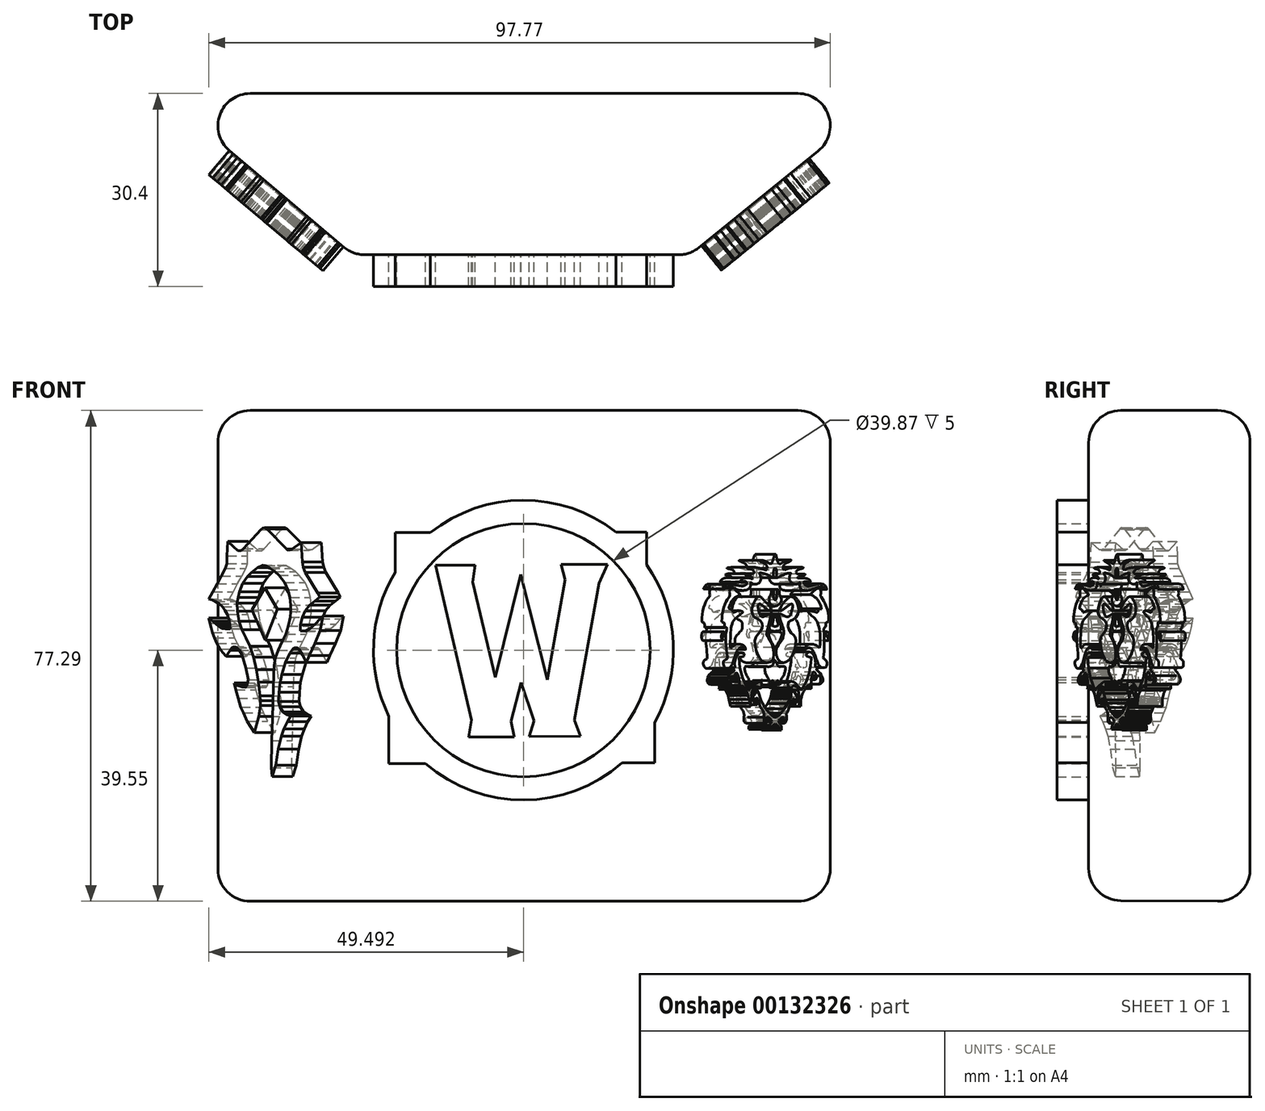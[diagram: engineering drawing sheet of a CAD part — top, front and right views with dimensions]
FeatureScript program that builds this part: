
annotation { "Feature Type Name" : "Feature", "Feature Type Description" : "" }
export const myFeature = defineFeature(function(context is Context, id is Id, definition is map)
    precondition{}
    {
        {
            var Q0;
            Q0=qCreatedBy(makeId("Front.planeOp"),FACE);
            var sketch = newSketch(context, id + "F0", { "sketchPlane" : qUnion([Q0])});
            skLineSegment(sketch, "E0.bottom", {"start": v(-46.33, 37.74) * mm, "end": v(68.1, 37.74) * mm});
            skLineSegment(sketch, "E0.top", {"start": v(-46.33, -39.59) * mm, "end": v(68.1, -39.59) * mm});
            skLineSegment(sketch, "E0.left", {"start": v(-46.33, 37.74) * mm, "end": v(-46.33, -39.59) * mm});
            skLineSegment(sketch, "E0.right", {"start": v(68.1, 37.74) * mm, "end": v(68.1, -39.59) * mm});
            skSolve(sketch);
        }
        {
            var Q0;
            Q0=makeQuery(id+"F0.imprint","IMPRINT",FACE,{"disambiguationData":[TD([[makeQuery(id+"F0.imprint","IMPRINT",EDGE,{"derivedFrom":sQuery(id+"F0.wireOp",EDGE,"E0.bottom")}),-1.0]])]});
            cPlane(context, id + "F1", {"entities" : qUnion([Q0]), "cplaneType" : CPlaneType.OFFSET, "offset" : 25.4 * mm, "width" : 152.4 * mm, "height" : 152.4 * mm});
        }
        {
            var Q0;
            Q0=qCreatedBy(id+"F1.planeOp",FACE);
            var sketch = newSketch(context, id + "F2", { "sketchPlane" : qUnion([Q0])});
            skLineSegment(sketch, "E1.bottom", {"start": v(-16.23, 37.74) * mm, "end": v(36.74, 37.74) * mm});
            skLineSegment(sketch, "E1.top", {"start": v(-16.23, -39.4) * mm, "end": v(36.74, -39.4) * mm});
            skLineSegment(sketch, "E1.left", {"start": v(-16.23, 37.74) * mm, "end": v(-16.23, -39.4) * mm});
            skLineSegment(sketch, "E1.right", {"start": v(36.74, 37.74) * mm, "end": v(36.74, -39.4) * mm});
            skSolve(sketch);
        }
        {
            var Q0;
            Q0=makeQuery(id+"F0.imprint","IMPRINT",FACE,{"disambiguationData":[TD([[makeQuery(id+"F0.imprint","IMPRINT",EDGE,{"derivedFrom":sQuery(id+"F0.wireOp",EDGE,"E0.bottom")}),-1.0]])]});
            var Q1;
            Q1=makeQuery(id+"F2.imprint","IMPRINT",FACE,{"disambiguationData":[TD([[makeQuery(id+"F2.imprint","IMPRINT",EDGE,{"derivedFrom":sQuery(id+"F2.wireOp",EDGE,"E1.bottom")}),-1.0]])]});
            loft(context, id + "F3", {"sheetProfilesArray" : [{ "sheetProfileEntities" : qUnion([Q0]) }, { "sheetProfileEntities" : qUnion([Q1]) }]});
        }
        {
            var Q0;
            Q0=makeQuery(id+"F3.opLoft","MID_CAP_EDGE",EDGE,{"disambiguationData":[OSD([sQuery(id+"F2.wireOp",EDGE,"E1.bottom"),sQuery(id+"F2.wireOp",EDGE,"E1.top"),sQuery(id+"F2.wireOp",EDGE,"E1.left")])],"capPos":1.0});
            var Q1;
            Q1=makeQuery(id+"F3.opLoft","MID_CAP_EDGE",EDGE,{"disambiguationData":[OSD([sQuery(id+"F2.wireOp",EDGE,"E1.bottom"),sQuery(id+"F2.wireOp",EDGE,"E1.top"),sQuery(id+"F2.wireOp",EDGE,"E1.right")])],"capPos":1.0});
            var Q2;
            Q2=makeQuery(id+"F3.opLoft","MID_CAP_EDGE",EDGE,{"disambiguationData":[OSD([sQuery(id+"F2.wireOp",EDGE,"E1.bottom"),sQuery(id+"F2.wireOp",EDGE,"E1.left"),sQuery(id+"F2.wireOp",EDGE,"E1.right")])],"capPos":1.0});
            var Q3;
            Q3=makeQuery(id+"F3.opLoft","SWEPT_EDGE",EDGE,{"disambiguationData":[OSD([sQuery(id+"F0.wireOp",EDGE,"E0.bottom"),sQuery(id+"F0.wireOp",EDGE,"E0.left"),sQuery(id+"F2.wireOp",EDGE,"E1.bottom"),sQuery(id+"F2.wireOp",EDGE,"E1.left")])]});
            var Q4;
            Q4=makeQuery(id+"F3.opLoft","SWEPT_EDGE",EDGE,{"disambiguationData":[OSD([sQuery(id+"F0.wireOp",EDGE,"E0.bottom"),sQuery(id+"F0.wireOp",EDGE,"E0.right"),sQuery(id+"F2.wireOp",EDGE,"E1.bottom"),sQuery(id+"F2.wireOp",EDGE,"E1.right")])]});
            var Q5;
            Q5=makeQuery(id+"F3.opLoft","SWEPT_EDGE",EDGE,{"disambiguationData":[OSD([sQuery(id+"F0.wireOp",EDGE,"E0.top"),sQuery(id+"F0.wireOp",EDGE,"E0.left"),sQuery(id+"F2.wireOp",EDGE,"E1.top"),sQuery(id+"F2.wireOp",EDGE,"E1.left")])]});
            var Q6;
            Q6=makeQuery(id+"F3.opLoft","MID_CAP_EDGE",EDGE,{"disambiguationData":[OSD([sQuery(id+"F2.wireOp",EDGE,"E1.top"),sQuery(id+"F2.wireOp",EDGE,"E1.left"),sQuery(id+"F2.wireOp",EDGE,"E1.right")])],"capPos":1.0});
            var Q7;
            Q7=makeQuery(id+"F3.opLoft","SWEPT_EDGE",EDGE,{"disambiguationData":[OSD([sQuery(id+"F0.wireOp",EDGE,"E0.top"),sQuery(id+"F0.wireOp",EDGE,"E0.right"),sQuery(id+"F2.wireOp",EDGE,"E1.top"),sQuery(id+"F2.wireOp",EDGE,"E1.right")])]});
            var Q8;
            Q8=makeQuery(id+"F3.opLoft","MID_CAP_EDGE",EDGE,{"disambiguationData":[OSD([sQuery(id+"F0.wireOp",EDGE,"E0.bottom"),sQuery(id+"F0.wireOp",EDGE,"E0.top"),sQuery(id+"F0.wireOp",EDGE,"E0.right")])],"capPos":0.0});
            var Q9;
            Q9=makeQuery(id+"F3.opLoft","MID_CAP_EDGE",EDGE,{"disambiguationData":[OSD([sQuery(id+"F0.wireOp",EDGE,"E0.bottom"),sQuery(id+"F0.wireOp",EDGE,"E0.top"),sQuery(id+"F0.wireOp",EDGE,"E0.left")])],"capPos":0.0});
            var Q10;
            Q10=makeQuery(id+"F3.opLoft","MID_CAP_EDGE",EDGE,{"disambiguationData":[OSD([sQuery(id+"F0.wireOp",EDGE,"E0.bottom"),sQuery(id+"F0.wireOp",EDGE,"E0.left"),sQuery(id+"F0.wireOp",EDGE,"E0.right")])],"capPos":0.0});
            var Q11;
            Q11=makeQuery(id+"F3.opLoft","MID_CAP_EDGE",EDGE,{"disambiguationData":[OSD([sQuery(id+"F0.wireOp",EDGE,"E0.top"),sQuery(id+"F0.wireOp",EDGE,"E0.left"),sQuery(id+"F0.wireOp",EDGE,"E0.right")])],"capPos":0.0});
            fillet(context, id + "F4", {"entities" : qUnion([Q0, Q1, Q2, Q3, Q4, Q5, Q6, Q7, Q8, Q9, Q10, Q11]), "radius" : 5.08 * mm, "tangentPropagation" : true, "allowEdgeOverflow" : false});
        }
        {
            var Q0;
            Q0=makeQuery(id+"F3.opLoft","CAP_FACE",FACE,{"disambiguationData":[OSD([makeQuery(id+"F2.imprint","IMPRINT",FACE,{"disambiguationData":[TD([[makeQuery(id+"F2.imprint","IMPRINT",EDGE,{"derivedFrom":sQuery(id+"F2.wireOp",EDGE,"E1.bottom")}),-1.0]])]})])],"isStart":true});
            var sketch = newSketch(context, id + "F5", { "sketchPlane" : qUnion([Q0])});
            skCircle(sketch, "E2", {"center": v(10.56, 0) * mm, "radius": 23.6 * mm});
            skCircle(sketch, "E3", {"center": v(10.56, 0) * mm, "radius": 19.94 * mm});
            skLineSegment(sketch, "E4", {"start": v(-3.27, 13.39) * mm, "end": v(2.38, -11) * mm});
            skLineSegment(sketch, "E5", {"start": v(2.38, -11) * mm, "end": v(1.94, -13.7) * mm});
            skLineSegment(sketch, "E6", {"start": v(1.94, -13.7) * mm, "end": v(9.12, -13.7) * mm});
            skLineSegment(sketch, "E7", {"start": v(9.12, -13.7) * mm, "end": v(8.63, -11.17) * mm});
            skLineSegment(sketch, "E8", {"start": v(8.63, -11.17) * mm, "end": v(10.22, -5.09) * mm});
            skLineSegment(sketch, "E9", {"start": v(10.22, -5.09) * mm, "end": v(12.24, -11.12) * mm});
            skLineSegment(sketch, "E10", {"start": v(12.24, -11.12) * mm, "end": v(11.48, -13.64) * mm});
            skLineSegment(sketch, "E11", {"start": v(11.48, -13.64) * mm, "end": v(19.54, -13.59) * mm});
            skLineSegment(sketch, "E12", {"start": v(19.54, -13.59) * mm, "end": v(18.55, -11) * mm});
            skLineSegment(sketch, "E13", {"start": v(18.55, -11) * mm, "end": v(22.44, 10.48) * mm});
            skLineSegment(sketch, "E14", {"start": v(22.44, 10.48) * mm, "end": v(23.76, 13.5) * mm});
            skLineSegment(sketch, "E15", {"start": v(23.76, 13.5) * mm, "end": v(16.47, 13.5) * mm});
            skLineSegment(sketch, "E16", {"start": v(16.47, 13.5) * mm, "end": v(17.12, 11.09) * mm});
            skLineSegment(sketch, "E17", {"start": v(17.12, 11.09) * mm, "end": v(14.33, -4.65) * mm});
            skLineSegment(sketch, "E18", {"start": v(14.33, -4.65) * mm, "end": v(10.1, 11.9) * mm});
            skLineSegment(sketch, "E19", {"start": v(10.1, 11.9) * mm, "end": v(6.16, -4.26) * mm});
            skLineSegment(sketch, "E20", {"start": v(6.16, -4.26) * mm, "end": v(2.6, 10.7) * mm});
            skLineSegment(sketch, "E21", {"start": v(2.6, 10.7) * mm, "end": v(2.98, 13.39) * mm});
            skLineSegment(sketch, "E22", {"start": v(2.98, 13.39) * mm, "end": v(-3.27, 13.39) * mm});
            skLineSegment(sketch, "E23", {"start": v(26.09, -17.77) * mm, "end": v(31.21, -17.77) * mm});
            skLineSegment(sketch, "E24", {"start": v(31.21, -17.77) * mm, "end": v(31.21, -11.42) * mm});
            skLineSegment(sketch, "E25", {"start": v(29.94, 13.46) * mm, "end": v(29.94, 18.6) * mm});
            skLineSegment(sketch, "E26", {"start": v(29.94, 18.6) * mm, "end": v(25.09, 18.6) * mm});
            skLineSegment(sketch, "E27", {"start": v(-9.62, 12.23) * mm, "end": v(-9.62, 18.49) * mm});
            skLineSegment(sketch, "E28", {"start": v(-9.62, 18.49) * mm, "end": v(-4.1, 18.49) * mm});
            skLineSegment(sketch, "E29", {"start": v(-10.6, -10.43) * mm, "end": v(-10.6, -17.86) * mm});
            skLineSegment(sketch, "E30", {"start": v(-10.6, -17.86) * mm, "end": v(-4.86, -17.86) * mm});
            skSolve(sketch);
        }
        {
            var Q0;
            Q0=makeQuery(id+"F3.opLoft","SWEPT_FACE",FACE,{"disambiguationData":[OSD([sQuery(id+"F0.wireOp",EDGE,"E0.bottom"),sQuery(id+"F0.wireOp",EDGE,"E0.top"),sQuery(id+"F0.wireOp",EDGE,"E0.right"),sQuery(id+"F2.wireOp",EDGE,"E1.bottom"),sQuery(id+"F2.wireOp",EDGE,"E1.top"),sQuery(id+"F2.wireOp",EDGE,"E1.right")])]});
            var sketch = newSketch(context, id + "F6", { "sketchPlane" : qUnion([Q0])});
            skLineSegment(sketch, "E31", {"start": v(20.34, -6.38) * mm, "end": v(19.23, -4.4) * mm});
            skLineSegment(sketch, "E32", {"start": v(19.23, -4.4) * mm, "end": v(18.66, -2.84) * mm});
            skLineSegment(sketch, "E33", {"start": v(18.66, -2.84) * mm, "end": v(18.47, -1.17) * mm});
            skLineSegment(sketch, "E34", {"start": v(18.47, -1.17) * mm, "end": v(18.9, -1.12) * mm});
            skLineSegment(sketch, "E35", {"start": v(18.9, -1.12) * mm, "end": v(19.46, -0.97) * mm});
            skLineSegment(sketch, "E36", {"start": v(19.46, -0.97) * mm, "end": v(19.52, -0.6) * mm});
            skLineSegment(sketch, "E37", {"start": v(19.52, -0.6) * mm, "end": v(19.1, -0.39) * mm});
            skLineSegment(sketch, "E38", {"start": v(19.1, -0.39) * mm, "end": v(18.67, -0.39) * mm});
            skLineSegment(sketch, "E39", {"start": v(18.67, -0.39) * mm, "end": v(18.3, -0.58) * mm});
            skLineSegment(sketch, "E40", {"start": v(18.3, -0.58) * mm, "end": v(17.8, -1.19) * mm});
            skLineSegment(sketch, "E41", {"start": v(17.8, -1.19) * mm, "end": v(17.6, -2) * mm});
            skLineSegment(sketch, "E42", {"start": v(17.6, -2) * mm, "end": v(17.64, -2.78) * mm});
            skLineSegment(sketch, "E43", {"start": v(17.64, -2.78) * mm, "end": v(17.16, -2.74) * mm});
            skLineSegment(sketch, "E44", {"start": v(17.16, -2.74) * mm, "end": v(17.02, -2.87) * mm});
            skLineSegment(sketch, "E45", {"start": v(17.02, -2.87) * mm, "end": v(17.09, -3) * mm});
            skLineSegment(sketch, "E46", {"start": v(17.09, -3) * mm, "end": v(17.33, -3.03) * mm});
            skLineSegment(sketch, "E47", {"start": v(17.33, -3.03) * mm, "end": v(17.4, -3.03) * mm});
            skLineSegment(sketch, "E48", {"start": v(17.4, -3.03) * mm, "end": v(17.5, -3.09) * mm});
            skLineSegment(sketch, "E49", {"start": v(17.5, -3.09) * mm, "end": v(17.5, -3.24) * mm});
            skLineSegment(sketch, "E50", {"start": v(17.5, -3.24) * mm, "end": v(17.26, -3.37) * mm});
            skLineSegment(sketch, "E51", {"start": v(17.26, -3.37) * mm, "end": v(16.95, -3.53) * mm});
            skLineSegment(sketch, "E52", {"start": v(16.95, -3.53) * mm, "end": v(16.54, -3.85) * mm});
            skLineSegment(sketch, "E53", {"start": v(16.54, -3.85) * mm, "end": v(16.17, -4.35) * mm});
            skLineSegment(sketch, "E54", {"start": v(16.17, -4.35) * mm, "end": v(16.06, -4.72) * mm});
            skLineSegment(sketch, "E55", {"start": v(16.06, -4.72) * mm, "end": v(16.11, -4.95) * mm});
            skLineSegment(sketch, "E56", {"start": v(16.11, -4.95) * mm, "end": v(16.27, -5.17) * mm});
            skLineSegment(sketch, "E57", {"start": v(16.27, -5.17) * mm, "end": v(16.5, -5.35) * mm});
            skLineSegment(sketch, "E58", {"start": v(16.5, -5.35) * mm, "end": v(16.86, -5.44) * mm});
            skLineSegment(sketch, "E59", {"start": v(16.86, -5.44) * mm, "end": v(16.74, -5.24) * mm});
            skLineSegment(sketch, "E60", {"start": v(16.74, -5.24) * mm, "end": v(16.6, -4.95) * mm});
            skLineSegment(sketch, "E61", {"start": v(16.6, -4.95) * mm, "end": v(16.56, -4.67) * mm});
            skLineSegment(sketch, "E62", {"start": v(16.56, -4.67) * mm, "end": v(16.59, -4.4) * mm});
            skLineSegment(sketch, "E63", {"start": v(16.59, -4.4) * mm, "end": v(16.76, -4.22) * mm});
            skLineSegment(sketch, "E64", {"start": v(16.76, -4.22) * mm, "end": v(16.92, -4.16) * mm});
            skLineSegment(sketch, "E65", {"start": v(16.92, -4.16) * mm, "end": v(17.22, -4.16) * mm});
            skLineSegment(sketch, "E66", {"start": v(17.22, -4.16) * mm, "end": v(17.36, -4.2) * mm});
            skLineSegment(sketch, "E67", {"start": v(17.36, -4.2) * mm, "end": v(17.46, -4.42) * mm});
            skLineSegment(sketch, "E68", {"start": v(17.46, -4.42) * mm, "end": v(17.55, -4.63) * mm});
            skLineSegment(sketch, "E69", {"start": v(17.55, -4.63) * mm, "end": v(17.64, -4.78) * mm});
            skLineSegment(sketch, "E70", {"start": v(17.64, -4.78) * mm, "end": v(17.8, -4.75) * mm});
            skLineSegment(sketch, "E71", {"start": v(17.8, -4.75) * mm, "end": v(17.95, -4.62) * mm});
            skLineSegment(sketch, "E72", {"start": v(17.95, -4.62) * mm, "end": v(18.13, -4.59) * mm});
            skLineSegment(sketch, "E73", {"start": v(18.13, -4.59) * mm, "end": v(18.06, -4.4) * mm});
            skLineSegment(sketch, "E74", {"start": v(18.06, -4.4) * mm, "end": v(17.9, -4.31) * mm});
            skLineSegment(sketch, "E75", {"start": v(17.9, -4.31) * mm, "end": v(17.67, -4.2) * mm});
            skLineSegment(sketch, "E76", {"start": v(17.67, -4.2) * mm, "end": v(17.57, -4.06) * mm});
            skLineSegment(sketch, "E77", {"start": v(17.57, -4.06) * mm, "end": v(17.57, -3.9) * mm});
            skLineSegment(sketch, "E78", {"start": v(17.57, -3.9) * mm, "end": v(17.79, -3.63) * mm});
            skLineSegment(sketch, "E79", {"start": v(17.79, -3.63) * mm, "end": v(17.94, -3.58) * mm});
            skLineSegment(sketch, "E80", {"start": v(17.94, -3.58) * mm, "end": v(18.1, -3.62) * mm});
            skLineSegment(sketch, "E81", {"start": v(18.1, -3.62) * mm, "end": v(18.28, -3.87) * mm});
            skLineSegment(sketch, "E82", {"start": v(18.28, -3.87) * mm, "end": v(18.42, -4.3) * mm});
            skLineSegment(sketch, "E83", {"start": v(18.42, -4.3) * mm, "end": v(18.53, -4.96) * mm});
            skLineSegment(sketch, "E84", {"start": v(18.53, -4.96) * mm, "end": v(18.53, -5.53) * mm});
            skLineSegment(sketch, "E85", {"start": v(18.53, -5.53) * mm, "end": v(18.5, -5.98) * mm});
            skLineSegment(sketch, "E86", {"start": v(18.5, -5.98) * mm, "end": v(18.45, -6.17) * mm});
            skLineSegment(sketch, "E87", {"start": v(18.45, -6.17) * mm, "end": v(18.64, -6.06) * mm});
            skLineSegment(sketch, "E88", {"start": v(18.64, -6.06) * mm, "end": v(18.72, -5.94) * mm});
            skLineSegment(sketch, "E89", {"start": v(18.72, -5.94) * mm, "end": v(18.82, -5.73) * mm});
            skLineSegment(sketch, "E90", {"start": v(18.82, -5.73) * mm, "end": v(18.94, -5.6) * mm});
            skLineSegment(sketch, "E91", {"start": v(18.94, -5.6) * mm, "end": v(19.05, -5.55) * mm});
            skLineSegment(sketch, "E92", {"start": v(19.05, -5.55) * mm, "end": v(19.29, -5.7) * mm});
            skLineSegment(sketch, "E93", {"start": v(19.29, -5.7) * mm, "end": v(19.52, -5.92) * mm});
            skLineSegment(sketch, "E94", {"start": v(19.52, -5.92) * mm, "end": v(19.85, -6.34) * mm});
            skLineSegment(sketch, "E95", {"start": v(19.85, -6.34) * mm, "end": v(20.09, -6.75) * mm});
            skLineSegment(sketch, "E96", {"start": v(20.09, -6.75) * mm, "end": v(20.29, -7.15) * mm});
            skLineSegment(sketch, "E97", {"start": v(20.29, -7.15) * mm, "end": v(20.52, -7.8) * mm});
            skLineSegment(sketch, "E98", {"start": v(20.52, -7.8) * mm, "end": v(20.68, -8.32) * mm});
            skLineSegment(sketch, "E99", {"start": v(20.68, -8.32) * mm, "end": v(20.82, -8.88) * mm});
            skLineSegment(sketch, "E100", {"start": v(20.82, -8.88) * mm, "end": v(20.88, -8.35) * mm});
            skLineSegment(sketch, "E101", {"start": v(20.88, -8.35) * mm, "end": v(20.98, -7.16) * mm});
            skLineSegment(sketch, "E102", {"start": v(20.98, -7.16) * mm, "end": v(21.2, -6.3) * mm});
            skLineSegment(sketch, "E103", {"start": v(21.2, -6.3) * mm, "end": v(21.5, -5.92) * mm});
            skLineSegment(sketch, "E104", {"start": v(21.5, -5.92) * mm, "end": v(21.71, -5.8) * mm});
            skLineSegment(sketch, "E105", {"start": v(21.71, -5.8) * mm, "end": v(21.9, -5.74) * mm});
            skLineSegment(sketch, "E106", {"start": v(21.9, -5.74) * mm, "end": v(22.16, -5.74) * mm});
            skLineSegment(sketch, "E107", {"start": v(22.16, -5.74) * mm, "end": v(22.39, -5.79) * mm});
            skLineSegment(sketch, "E108", {"start": v(22.39, -5.79) * mm, "end": v(22.68, -5.89) * mm});
            skLineSegment(sketch, "E109", {"start": v(22.68, -5.89) * mm, "end": v(22.84, -5.99) * mm});
            skLineSegment(sketch, "E110", {"start": v(22.84, -5.99) * mm, "end": v(22.86, -5.93) * mm});
            skLineSegment(sketch, "E111", {"start": v(22.86, -5.93) * mm, "end": v(22.91, -5.9) * mm});
            skLineSegment(sketch, "E112", {"start": v(22.91, -5.9) * mm, "end": v(23.04, -5.9) * mm});
            skLineSegment(sketch, "E113", {"start": v(23.04, -5.9) * mm, "end": v(23.08, -5.52) * mm});
            skLineSegment(sketch, "E114", {"start": v(23.08, -5.52) * mm, "end": v(23.1, -5.3) * mm});
            skLineSegment(sketch, "E115", {"start": v(23.1, -5.3) * mm, "end": v(23.01, -5.11) * mm});
            skLineSegment(sketch, "E116", {"start": v(23.01, -5.11) * mm, "end": v(22.87, -5) * mm});
            skLineSegment(sketch, "E117", {"start": v(22.87, -5) * mm, "end": v(22.55, -5) * mm});
            skLineSegment(sketch, "E118", {"start": v(22.55, -5) * mm, "end": v(21.98, -5.2) * mm});
            skLineSegment(sketch, "E119", {"start": v(21.98, -5.2) * mm, "end": v(21.28, -5.62) * mm});
            skLineSegment(sketch, "E120", {"start": v(21.28, -5.62) * mm, "end": v(20.76, -6) * mm});
            skLineSegment(sketch, "E121", {"start": v(20.76, -6) * mm, "end": v(20.34, -6.38) * mm});
            skLineSegment(sketch, "E122", {"start": v(21.35, -7.22) * mm, "end": v(21.57, -7.1) * mm});
            skLineSegment(sketch, "E123", {"start": v(21.57, -7.1) * mm, "end": v(21.72, -6.91) * mm});
            skLineSegment(sketch, "E124", {"start": v(21.72, -6.91) * mm, "end": v(21.9, -6.55) * mm});
            skLineSegment(sketch, "E125", {"start": v(21.9, -6.55) * mm, "end": v(22.2, -6.25) * mm});
            skLineSegment(sketch, "E126", {"start": v(22.2, -6.25) * mm, "end": v(22.5, -6.85) * mm});
            skLineSegment(sketch, "E127", {"start": v(22.5, -6.85) * mm, "end": v(22.92, -7.82) * mm});
            skLineSegment(sketch, "E128", {"start": v(22.92, -7.82) * mm, "end": v(23.23, -8.38) * mm});
            skLineSegment(sketch, "E129", {"start": v(23.23, -8.38) * mm, "end": v(23.72, -9.04) * mm});
            skLineSegment(sketch, "E130", {"start": v(23.72, -9.04) * mm, "end": v(24.27, -9.6) * mm});
            skLineSegment(sketch, "E131", {"start": v(24.27, -9.6) * mm, "end": v(24.66, -9.95) * mm});
            skLineSegment(sketch, "E132", {"start": v(24.66, -9.95) * mm, "end": v(25.17, -10.31) * mm});
            skLineSegment(sketch, "E133", {"start": v(25.17, -10.31) * mm, "end": v(25.5, -10.49) * mm});
            skLineSegment(sketch, "E134", {"start": v(25.5, -10.49) * mm, "end": v(25.72, -10.55) * mm});
            skLineSegment(sketch, "E135", {"start": v(25.72, -10.55) * mm, "end": v(26, -10.55) * mm});
            skLineSegment(sketch, "E136", {"start": v(26, -10.55) * mm, "end": v(26.46, -10.32) * mm});
            skLineSegment(sketch, "E137", {"start": v(26.46, -10.32) * mm, "end": v(26.96, -9.94) * mm});
            skLineSegment(sketch, "E138", {"start": v(26.96, -9.94) * mm, "end": v(27.64, -9.27) * mm});
            skLineSegment(sketch, "E139", {"start": v(27.64, -9.27) * mm, "end": v(28.3, -8.44) * mm});
            skLineSegment(sketch, "E140", {"start": v(28.3, -8.44) * mm, "end": v(28.82, -7.64) * mm});
            skLineSegment(sketch, "E141", {"start": v(28.82, -7.64) * mm, "end": v(29.02, -7.24) * mm});
            skLineSegment(sketch, "E142", {"start": v(29.02, -7.24) * mm, "end": v(29.06, -6.82) * mm});
            skLineSegment(sketch, "E143", {"start": v(29.06, -6.82) * mm, "end": v(29.14, -6.47) * mm});
            skLineSegment(sketch, "E144", {"start": v(29.14, -6.47) * mm, "end": v(29.22, -6.3) * mm});
            skLineSegment(sketch, "E145", {"start": v(29.22, -6.3) * mm, "end": v(29.42, -6.24) * mm});
            skLineSegment(sketch, "E146", {"start": v(29.42, -6.24) * mm, "end": v(30.3, -7.38) * mm});
            skLineSegment(sketch, "E147", {"start": v(30.3, -7.38) * mm, "end": v(30.25, -7.72) * mm});
            skLineSegment(sketch, "E148", {"start": v(30.25, -7.72) * mm, "end": v(30.16, -8.08) * mm});
            skLineSegment(sketch, "E149", {"start": v(30.16, -8.08) * mm, "end": v(30, -8.36) * mm});
            skLineSegment(sketch, "E150", {"start": v(30, -8.36) * mm, "end": v(29.82, -8.54) * mm});
            skLineSegment(sketch, "E151", {"start": v(29.82, -8.54) * mm, "end": v(29.57, -8.61) * mm});
            skLineSegment(sketch, "E152", {"start": v(29.57, -8.61) * mm, "end": v(29.41, -8.62) * mm});
            skLineSegment(sketch, "E153", {"start": v(29.41, -8.62) * mm, "end": v(29.44, -8.44) * mm});
            skLineSegment(sketch, "E154", {"start": v(29.44, -8.44) * mm, "end": v(29.52, -8.27) * mm});
            skLineSegment(sketch, "E155", {"start": v(29.52, -8.27) * mm, "end": v(29.63, -8.07) * mm});
            skLineSegment(sketch, "E156", {"start": v(29.63, -8.07) * mm, "end": v(29.7, -7.87) * mm});
            skLineSegment(sketch, "E157", {"start": v(29.7, -7.87) * mm, "end": v(29.7, -7.57) * mm});
            skLineSegment(sketch, "E158", {"start": v(29.7, -7.57) * mm, "end": v(29.37, -7.78) * mm});
            skLineSegment(sketch, "E159", {"start": v(29.37, -7.78) * mm, "end": v(29.08, -8.18) * mm});
            skLineSegment(sketch, "E160", {"start": v(29.08, -8.18) * mm, "end": v(28.85, -8.62) * mm});
            skLineSegment(sketch, "E161", {"start": v(28.85, -8.62) * mm, "end": v(28.64, -9.06) * mm});
            skLineSegment(sketch, "E162", {"start": v(28.64, -9.06) * mm, "end": v(28.37, -9.6) * mm});
            skLineSegment(sketch, "E163", {"start": v(28.37, -9.6) * mm, "end": v(28.17, -9.87) * mm});
            skLineSegment(sketch, "E164", {"start": v(28.17, -9.87) * mm, "end": v(28.03, -10.02) * mm});
            skLineSegment(sketch, "E165", {"start": v(28.03, -10.02) * mm, "end": v(28.1, -10.42) * mm});
            skLineSegment(sketch, "E166", {"start": v(28.1, -10.42) * mm, "end": v(28.09, -10.91) * mm});
            skLineSegment(sketch, "E167", {"start": v(28.09, -10.91) * mm, "end": v(28, -11.23) * mm});
            skLineSegment(sketch, "E168", {"start": v(28, -11.23) * mm, "end": v(27.9, -11.42) * mm});
            skLineSegment(sketch, "E169", {"start": v(27.9, -11.42) * mm, "end": v(27.74, -11.53) * mm});
            skLineSegment(sketch, "E170", {"start": v(27.74, -11.53) * mm, "end": v(27.63, -11.42) * mm});
            skLineSegment(sketch, "E171", {"start": v(27.63, -11.42) * mm, "end": v(27.66, -11.08) * mm});
            skLineSegment(sketch, "E172", {"start": v(27.66, -11.08) * mm, "end": v(27.68, -10.75) * mm});
            skLineSegment(sketch, "E173", {"start": v(27.68, -10.75) * mm, "end": v(27.53, -10.65) * mm});
            skLineSegment(sketch, "E174", {"start": v(27.53, -10.65) * mm, "end": v(27.32, -10.65) * mm});
            skLineSegment(sketch, "E175", {"start": v(27.32, -10.65) * mm, "end": v(27.06, -10.7) * mm});
            skLineSegment(sketch, "E176", {"start": v(27.06, -10.7) * mm, "end": v(26.45, -11.07) * mm});
            skLineSegment(sketch, "E177", {"start": v(26.45, -11.07) * mm, "end": v(26.54, -11.32) * mm});
            skLineSegment(sketch, "E178", {"start": v(26.54, -11.32) * mm, "end": v(26.77, -11.59) * mm});
            skLineSegment(sketch, "E179", {"start": v(26.77, -11.59) * mm, "end": v(26.96, -11.86) * mm});
            skLineSegment(sketch, "E180", {"start": v(26.96, -11.86) * mm, "end": v(27.04, -12.07) * mm});
            skLineSegment(sketch, "E181", {"start": v(27.04, -12.07) * mm, "end": v(27.07, -12.28) * mm});
            skLineSegment(sketch, "E182", {"start": v(27.07, -12.28) * mm, "end": v(27.09, -12.58) * mm});
            skLineSegment(sketch, "E183", {"start": v(27.09, -12.58) * mm, "end": v(26.79, -12.4) * mm});
            skLineSegment(sketch, "E184", {"start": v(26.79, -12.4) * mm, "end": v(26.52, -12.2) * mm});
            skLineSegment(sketch, "E185", {"start": v(26.52, -12.2) * mm, "end": v(26.2, -11.9) * mm});
            skLineSegment(sketch, "E186", {"start": v(26.2, -11.9) * mm, "end": v(25.83, -11.6) * mm});
            skLineSegment(sketch, "E187", {"start": v(25.83, -11.6) * mm, "end": v(25.57, -11.7) * mm});
            skLineSegment(sketch, "E188", {"start": v(25.57, -11.7) * mm, "end": v(25.3, -11.98) * mm});
            skLineSegment(sketch, "E189", {"start": v(25.3, -11.98) * mm, "end": v(25.04, -12.3) * mm});
            skLineSegment(sketch, "E190", {"start": v(25.04, -12.3) * mm, "end": v(24.73, -12.46) * mm});
            skLineSegment(sketch, "E191", {"start": v(24.73, -12.46) * mm, "end": v(24.5, -12.48) * mm});
            skLineSegment(sketch, "E192", {"start": v(24.5, -12.48) * mm, "end": v(24.52, -12.14) * mm});
            skLineSegment(sketch, "E193", {"start": v(24.52, -12.14) * mm, "end": v(24.63, -11.86) * mm});
            skLineSegment(sketch, "E194", {"start": v(24.63, -11.86) * mm, "end": v(24.9, -11.52) * mm});
            skLineSegment(sketch, "E195", {"start": v(24.9, -11.52) * mm, "end": v(25.11, -11.24) * mm});
            skLineSegment(sketch, "E196", {"start": v(25.11, -11.24) * mm, "end": v(24.96, -10.97) * mm});
            skLineSegment(sketch, "E197", {"start": v(24.96, -10.97) * mm, "end": v(24.72, -10.77) * mm});
            skFitSpline(sketch, "E198", {"points": [v(28.46, -5.7) * mm, v(28.45, -5.11) * mm, v(28.54, -5.1) * mm, v(28.71, -5.02) * mm, v(29.09, -4.94) * mm, v(29.72, -5.1) * mm, v(30.45, -5.68) * mm, v(31.15, -6.34) * mm, v(31.26, -6.24) * mm, v(32.15, -4.78) * mm, v(32.76, -3.23) * mm, v(33.1, -1.14) * mm, v(33, -1.1) * mm, v(32.42, -1.03) * mm, v(32.17, -0.95) * mm, v(32.04, -0.76) * mm, v(32.37, -0.4) * mm, v(32.82, -0.31) * mm, v(33.28, -0.47) * mm, v(33.82, -1.22) * mm, v(33.96, -1.8) * mm, v(33.95, -2.27) * mm, v(33.9, -2.57) * mm, v(34.26, -2.67) * mm, v(34.5, -2.72) * mm, v(34.48, -2.89) * mm, v(34.24, -2.96) * mm, v(34.09, -3.05) * mm, v(34.37, -3.26) * mm, v(35.02, -3.8) * mm, v(35.46, -4.4) * mm, v(35.49, -4.83) * mm, v(35.31, -5.08) * mm, v(34.92, -5.3) * mm, v(34.7, -5.36) * mm, v(34.9, -5.09) * mm, v(35, -4.7) * mm, v(34.96, -4.3) * mm, v(34.64, -4.06) * mm, v(34.38, -4.08) * mm, v(34, -4.6) * mm, v(33.75, -4.67) * mm, v(33.57, -4.6) * mm, v(33.55, -4.37) * mm, v(33.92, -4.15) * mm, v(34, -3.98) * mm, v(33.94, -3.62) * mm, v(33.59, -3.44) * mm, v(33.13, -4.41) * mm, v(33.1, -6.05) * mm, v(33.09, -6.09) * mm, v(32.87, -5.94) * mm, v(32.82, -5.82) * mm, v(32.75, -5.6) * mm, v(32.6, -5.5) * mm, v(31.85, -6.13) * mm, v(31.26, -7.08) * mm, v(30.95, -8.2) * mm, v(30.92, -8.87) * mm, v(30.66, -8.41) * mm, v(30.57, -7.58) * mm, v(30.56, -6.76) * mm, v(30.46, -6.23) * mm, v(30.25, -5.81) * mm, v(29.77, -5.65) * mm, v(29.4, -5.65) * mm, v(29.08, -5.9) * mm, v(28.76, -5.9) * mm, v(28.46, -5.7) * mm]});
            skFitSpline(sketch, "E199", {"points": [v(31.81, 0.1) * mm, v(32.33, 0.32) * mm, v(32.98, 0.3) * mm, v(33.62, -0.3) * mm, v(34.15, -1.42) * mm, v(34.58, -2.28) * mm, v(34.94, -2.61) * mm, v(35.32, -2.77) * mm, v(35.65, -2.77) * mm, v(36.17, -2.6) * mm, v(36.29, -2.12) * mm, v(36.18, -1.74) * mm, v(35.49, -1.24) * mm, v(35.52, -1.1) * mm, v(35.73, 0.59) * mm, v(35.73, 2.2) * mm, v(35.65, 3.38) * mm, v(35.69, 3.43) * mm, v(35.9, 3.62) * mm, v(36.03, 3.9) * mm, v(36.02, 4.28) * mm, v(36.11, 4.3) * mm, v(36.4, 4.4) * mm, v(36.62, 4.62) * mm, v(36.5, 5.95) * mm, v(36.1, 6.98) * mm, v(35.15, 8.37) * mm, v(34.96, 8.58) * mm, v(35.04, 8.73) * mm, v(34.96, 9.55) * mm, v(34.27, 9.68) * mm, v(32.94, 8.75) * mm, v(33.01, 8.74) * mm, v(33.62, 8.46) * mm, v(34.22, 8.08) * mm, v(34.66, 7.64) * mm, v(34.99, 7.06) * mm, v(35.14, 6.5) * mm, v(35.06, 6.48) * mm, v(34.82, 6.48) * mm, v(34.62, 6.32) * mm, v(34.4, 6.03) * mm, v(34.3, 5.93) * mm, v(33.99, 6) * mm, v(33.2, 6.18) * mm, v(32.68, 6.14) * mm, v(32.43, 6.03) * mm, v(32.7, 5.76) * mm, v(33.2, 5.4) * mm, v(33.76, 5.04) * mm, v(34.29, 4.47) * mm, v(34.68, 3.58) * mm, v(34.9, 1.99) * mm, v(34.78, 0.33) * mm, v(34.7, 0.39) * mm, v(34.24, 0.7) * mm, v(33.3, 0.93) * mm, v(32.54, 0.87) * mm, v(32.03, 0.6) * mm, v(31.81, 0.1) * mm]});
            skFitSpline(sketch, "E200", {"points": [v(36.53, 1.5) * mm, v(36.61, 1.57) * mm, v(36.7, 1.98) * mm, v(36.72, 2.45) * mm, v(36.52, 2.8) * mm, v(36.18, 2.88) * mm, v(36.05, 2.65) * mm, v(36.1, 2.44) * mm, v(36.23, 2.22) * mm, v(36.38, 2.02) * mm, v(36.51, 1.76) * mm, v(36.53, 1.5) * mm]});
            skFitSpline(sketch, "E201", {"points": [v(16.67, -2.68) * mm, v(16.94, -2.44) * mm, v(17.61, -1.07) * mm, v(18.1, -0.08) * mm, v(18.2, 0) * mm, v(18.62, 0.33) * mm, v(19.16, 0.41) * mm, v(19.8, 0.09) * mm, v(19.73, 0.4) * mm, v(19.34, 0.76) * mm, v(18.45, 0.93) * mm, v(17.48, 0.76) * mm, v(16.8, 0.33) * mm, v(16.75, 2.17) * mm, v(16.89, 3.5) * mm, v(17.3, 4.54) * mm, v(18.2, 5.29) * mm, v(19.02, 5.79) * mm, v(19.22, 6) * mm, v(18.87, 6.17) * mm, v(18.2, 6.18) * mm, v(17.27, 5.92) * mm, v(17.26, 6.03) * mm, v(16.72, 6.5) * mm, v(16.45, 6.58) * mm, v(16.97, 7.64) * mm, v(17.89, 8.37) * mm, v(18.71, 8.74) * mm, v(17.8, 9.35) * mm, v(17.65, 9.75) * mm, v(17.83, 9.64) * mm, v(18.51, 9.45) * mm, v(19.8, 9.43) * mm, v(20.62, 9.78) * mm, v(20.85, 10.38) * mm, v(20.82, 10.7) * mm, v(21.05, 10.55) * mm, v(21.6, 10.37) * mm, v(22.17, 10.42) * mm, v(22.58, 10.61) * mm, v(22.84, 10.95) * mm, v(22.94, 11.32) * mm, v(22.8, 11.68) * mm, v(22.65, 11.95) * mm, v(22.67, 12.16) * mm, v(23.2, 12.11) * mm, v(24.28, 11.84) * mm, v(25.46, 11.41) * mm, v(25.45, 11.75) * mm, v(25.49, 12.51) * mm, v(25.66, 12.83) * mm, v(25.92, 12.88) * mm, v(26.06, 12.55) * mm, v(26.1, 11.41) * mm, v(26.36, 11.44) * mm, v(27.74, 11.94) * mm, v(28.4, 12.1) * mm, v(29, 12.1) * mm, v(28.85, 11.94) * mm, v(28.7, 11.43) * mm, v(28.73, 11.05) * mm, v(29.2, 10.55) * mm, v(30.08, 10.4) * mm, v(30.73, 10.6) * mm, v(30.81, 10.67) * mm, v(30.8, 9.93) * mm, v(31.57, 9.43) * mm, v(32.97, 9.47) * mm, v(34.23, 9.84) * mm, v(35, 9.98) * mm, v(35.72, 9.83) * mm, v(36.22, 9.54) * mm, v(36.06, 9.97) * mm, v(35.63, 10.34) * mm, v(34.39, 10.4) * mm, v(33.06, 10.14) * mm, v(32.04, 10.15) * mm, v(31.7, 10.44) * mm, v(31.53, 10.67) * mm, v(31.7, 10.77) * mm, v(32.15, 10.76) * mm, v(32.77, 10.71) * mm, v(32.96, 10.77) * mm, v(32.73, 11.05) * mm, v(32.22, 11.26) * mm, v(31.18, 11.35) * mm, v(30.3, 11.38) * mm, v(30.47, 11.5) * mm, v(31.12, 11.66) * mm, v(31.6, 11.77) * mm, v(31.87, 11.89) * mm, v(31.72, 11.97) * mm, v(31.3, 11.98) * mm, v(30.42, 11.99) * mm, v(30.03, 12.24) * mm, v(30.26, 12.55) * mm, v(30.84, 12.76) * mm, v(31.34, 12.87) * mm, v(31.52, 12.96) * mm, v(31.12, 13.04) * mm, v(29.67, 13) * mm, v(28.2, 12.79) * mm, v(27.47, 12.68) * mm, v(27.5, 13.27) * mm, v(28.03, 13.7) * mm, v(28.66, 13.93) * mm, v(29.05, 14.17) * mm, v(28.68, 14.17) * mm, v(27.57, 13.94) * mm, v(26.7, 13.56) * mm, v(26.17, 14.25) * mm, v(25.9, 15.06) * mm, v(25.67, 14.9) * mm, v(25.22, 13.86) * mm, v(24.92, 13.6) * mm, v(23.93, 13.94) * mm, v(23.21, 14.13) * mm, v(22.51, 14.12) * mm, v(22.89, 13.93) * mm, v(23.68, 13.64) * mm, v(24.1, 13.22) * mm, v(24.2, 12.84) * mm, v(24.1, 12.87) * mm, v(23.98, 12.62) * mm, v(23.57, 12.69) * mm, v(22.2, 12.98) * mm, v(21.13, 13.05) * mm, v(20.07, 12.9) * mm, v(20.9, 12.73) * mm, v(21.36, 12.58) * mm, v(21.54, 12.2) * mm, v(21.28, 12.02) * mm, v(20.85, 12.01) * mm, v(20.16, 12) * mm, v(19.79, 11.85) * mm, v(20.34, 11.66) * mm, v(21.03, 11.53) * mm, v(21.2, 11.36) * mm, v(21.2, 11.2) * mm, v(20.8, 11.33) * mm, v(19.82, 11.38) * mm, v(19.13, 11.16) * mm, v(18.72, 10.71) * mm, v(19.34, 10.77) * mm, v(19.78, 10.84) * mm, v(20, 10.68) * mm, v(20.02, 10.44) * mm, v(19.7, 10.2) * mm, v(19.16, 10.08) * mm, v(18.17, 10.2) * mm, v(16.97, 10.36) * mm, v(16.36, 10.4) * mm, v(15.77, 10.2) * mm, v(15.36, 9.64) * mm, v(15.88, 9.8) * mm, v(16.37, 9.97) * mm, v(16.77, 10.06) * mm, v(17.15, 9.97) * mm, v(17.39, 9.77) * mm, v(17.1, 9.74) * mm, v(16.76, 9.63) * mm, v(16.54, 9.2) * mm, v(16.6, 8.54) * mm, v(16.25, 8.15) * mm, v(15.33, 6.6) * mm, v(15.01, 4.52) * mm, v(15.12, 4.4) * mm, v(15.37, 4.33) * mm, v(15.56, 4.05) * mm, v(15.57, 3.56) * mm, v(15.75, 3.58) * mm, v(15.98, 3.48) * mm, v(15.9, 3.02) * mm, v(15.8, 1.3) * mm, v(16.1, -1.32) * mm, v(15.92, -1.42) * mm, v(15.42, -1.7) * mm, v(15.31, -1.86) * mm, v(15.33, -2.34) * mm, v(15.62, -2.73) * mm, v(16.1, -2.9) * mm, v(16.54, -2.8) * mm, v(16.67, -2.68) * mm]});
            skFitSpline(sketch, "E202", {"points": [v(15.2, 1.5) * mm, v(15.15, 1.76) * mm, v(15.21, 2.08) * mm, v(15.48, 2.38) * mm, v(15.55, 2.77) * mm, v(15.26, 2.92) * mm, v(15.06, 2.72) * mm, v(14.92, 2.26) * mm, v(14.95, 1.85) * mm, v(15.2, 1.5) * mm]});
            skFitSpline(sketch, "E203", {"points": [v(25.88, 7.9) * mm, v(26.05, 8.15) * mm, v(26.11, 8.65) * mm, v(26.15, 9.22) * mm, v(26.22, 9.5) * mm, v(26.47, 9.55) * mm, v(26.62, 9.3) * mm, v(26.62, 8.9) * mm, v(26.64, 8.73) * mm, v(26.85, 8.5) * mm, v(27.04, 8.07) * mm, v(27.01, 7.7) * mm, v(26.75, 7.34) * mm, v(26.15, 7.01) * mm, v(25.62, 6.92) * mm, v(25.09, 7.06) * mm, v(24.72, 7.36) * mm, v(24.56, 7.9) * mm, v(24.7, 8.43) * mm, v(24.98, 8.88) * mm, v(25.04, 9.56) * mm, v(25.18, 9.54) * mm, v(25.33, 9.5) * mm, v(25.48, 9.21) * mm, v(25.47, 8.73) * mm, v(25.49, 8.17) * mm, v(25.6, 8) * mm, v(25.75, 7.9) * mm, v(25.88, 7.9) * mm]});
            skFitSpline(sketch, "E204", {"points": [v(24.9, 6.4) * mm, v(24.74, 6.83) * mm, v(24.35, 7.2) * mm, v(23.56, 7.84) * mm, v(23, 8.28) * mm, v(22.67, 8.4) * mm, v(22.36, 8.4) * mm, v(21.93, 8.1) * mm, v(21.43, 7.4) * mm, v(21.06, 6.25) * mm, v(21.17, 5.68) * mm, v(21.52, 5.23) * mm, v(22.38, 4.83) * mm, v(23.1, 4.4) * mm, v(23.18, 3.98) * mm, v(23.21, 3.61) * mm, v(22.9, 3.04) * mm, v(22.22, 2.45) * mm, v(21.73, 1.8) * mm, v(21.75, 0.68) * mm, v(22.2, -0.57) * mm, v(22.84, -1.46) * mm, v(23.38, -1.82) * mm, v(24.1, -1.99) * mm, v(24.86, -1.82) * mm, v(25.36, -1.4) * mm, v(25.5, -0.63) * mm, v(25.26, 0.6) * mm, v(24.64, 1.74) * mm, v(24.09, 2.36) * mm, v(24.38, 3.6) * mm, v(24.89, 5.35) * mm, v(24.95, 5.68) * mm, v(24.71, 5.68) * mm, v(23.73, 5.35) * mm, v(23.11, 5.24) * mm, v(22.63, 5.77) * mm, v(22.33, 6.73) * mm, v(22.49, 7.24) * mm, v(22.98, 7.15) * mm, v(23.4, 6.93) * mm, v(24.09, 6.45) * mm, v(24.45, 6.26) * mm, v(24.88, 6.2) * mm, v(24.9, 6.4) * mm]});
            skFitSpline(sketch, "E205", {"points": [v(25.49, 5.6) * mm, v(25.18, 5.12) * mm, v(24.77, 4.18) * mm, v(24.6, 3.45) * mm, v(24.9, 3.12) * mm, v(25.44, 2.99) * mm, v(26.14, 3) * mm, v(26.56, 3.04) * mm, v(26.96, 3.28) * mm, v(26.92, 3.99) * mm, v(26.49, 5.04) * mm, v(26.1, 5.47) * mm, v(26.09, 5.13) * mm, v(26.3, 4.4) * mm, v(26.38, 3.87) * mm, v(25.71, 3.74) * mm, v(25.4, 3.79) * mm, v(25.23, 3.98) * mm, v(25.36, 4.58) * mm, v(25.49, 5.09) * mm, v(25.49, 5.6) * mm]});
            skFitSpline(sketch, "E206", {"points": [v(25.7, 2.9) * mm, v(24.93, 2.87) * mm, v(24.53, 2.64) * mm, v(24.65, 1.95) * mm, v(25.13, 1.17) * mm, v(25.58, 0.57) * mm, v(25.92, 0.41) * mm, v(26.46, 1.17) * mm, v(26.72, 1.5) * mm, v(27.07, 2.16) * mm, v(27.12, 2.7) * mm, v(25.7, 2.9) * mm]});
            skFitSpline(sketch, "E207", {"points": [v(26.1, -0.86) * mm, v(25.98, -0.44) * mm, v(26.07, 0.2) * mm, v(26.49, 0.82) * mm, v(27.08, 1.42) * mm, v(27.45, 2.13) * mm, v(27.52, 2.9) * mm, v(27.37, 3.5) * mm, v(27.14, 4.07) * mm, v(26.93, 4.54) * mm, v(26.75, 5.01) * mm, v(26.68, 5.68) * mm, v(27.47, 5.5) * mm, v(28.17, 5.23) * mm, v(28.6, 5.27) * mm, v(28.99, 5.69) * mm, v(29.15, 6.2) * mm, v(29.32, 7.17) * mm, v(28.82, 7.21) * mm, v(27.92, 6.7) * mm, v(27.36, 6.36) * mm, v(26.87, 6.23) * mm, v(26.9, 6.66) * mm, v(27.55, 7.5) * mm, v(28.46, 8.2) * mm, v(28.9, 8.42) * mm, v(29.45, 8.3) * mm, v(29.96, 7.87) * mm, v(30.43, 6.97) * mm, v(30.54, 6.24) * mm, v(30.42, 5.62) * mm, v(29.67, 4.96) * mm, v(28.95, 4.64) * mm, v(28.55, 4.44) * mm, v(28.39, 3.73) * mm, v(28.8, 2.9) * mm, v(29.46, 2.42) * mm, v(29.77, 2.12) * mm, v(29.96, 1.63) * mm, v(29.87, 0.4) * mm, v(29.34, -0.71) * mm, v(28.63, -1.55) * mm, v(27.93, -1.9) * mm, v(27.36, -1.97) * mm, v(26.7, -1.74) * mm, v(26.23, -1.21) * mm, v(26.1, -0.86) * mm]});
            skFitSpline(sketch, "E208", {"points": [v(25.67, -1.6) * mm, v(25.92, -1.76) * mm, v(26.15, -2.18) * mm, v(26.36, -2.47) * mm, v(26.6, -2.6) * mm, v(27.18, -2.56) * mm, v(27.82, -2.65) * mm, v(27.84, -3.15) * mm, v(27.63, -3.75) * mm, v(27.3, -4.27) * mm, v(26.98, -4.75) * mm, v(26.79, -5.42) * mm, v(26.58, -5.24) * mm, v(26.45, -4.85) * mm, v(26.34, -4.77) * mm, v(26.13, -4.87) * mm, v(25.98, -5.27) * mm, v(25.82, -5.8) * mm, v(25.62, -5.57) * mm, v(25.46, -4.94) * mm, v(25.3, -4.77) * mm, v(25.08, -4.92) * mm, v(24.83, -5.47) * mm, v(24.7, -5.1) * mm, v(24.4, -4.43) * mm, v(23.99, -3.85) * mm, v(23.72, -3.23) * mm, v(23.8, -2.58) * mm, v(24.34, -2.62) * mm, v(24.97, -2.52) * mm, v(25.42, -2.21) * mm, v(25.67, -1.6) * mm]});
            skFitSpline(sketch, "E209", {"points": [v(24.72, -10.77) * mm, v(24.35, -10.6) * mm, v(23.85, -10.77) * mm, v(23.96, -11.24) * mm, v(23.98, -11.48) * mm, v(23.67, -11.4) * mm, v(23.51, -11.03) * mm, v(23.55, -10.3) * mm, v(23.42, -9.73) * mm, v(22.96, -9.13) * mm, v(22.65, -8.61) * mm, v(22.47, -8.02) * mm, v(22.3, -7.73) * mm, v(22, -7.55) * mm, v(21.88, -7.8) * mm, v(22.06, -8.25) * mm, v(22.14, -8.6) * mm, v(21.72, -8.42) * mm, v(21.42, -8.04) * mm, v(21.35, -7.22) * mm], "startDerivative": vector(-6.46, 4.82) * mm, "endDerivative": vector(0, 13.17) * mm});
            skSolve(sketch);
        }
        {
            var Q0;
            Q0=makeQuery(id+"F3.opLoft","SWEPT_FACE",FACE,{"disambiguationData":[OSD([sQuery(id+"F0.wireOp",EDGE,"E0.bottom"),sQuery(id+"F0.wireOp",EDGE,"E0.top"),sQuery(id+"F0.wireOp",EDGE,"E0.left"),sQuery(id+"F2.wireOp",EDGE,"E1.bottom"),sQuery(id+"F2.wireOp",EDGE,"E1.top"),sQuery(id+"F2.wireOp",EDGE,"E1.left")])]});
            var sketch = newSketch(context, id + "F7", { "sketchPlane" : qUnion([Q0])});
            skLineSegment(sketch, "E210", {"start": v(-9.91, 1.57) * mm, "end": v(-7.4, 6.47) * mm});
            skLineSegment(sketch, "E211", {"start": v(-7.4, 6.47) * mm, "end": v(-9.95, 9.81) * mm});
            skLineSegment(sketch, "E212", {"start": v(-9.95, 9.81) * mm, "end": v(-12.69, 6.3) * mm});
            skLineSegment(sketch, "E213", {"start": v(-12.69, 6.3) * mm, "end": v(-9.91, 1.57) * mm});
            skLineSegment(sketch, "E214", {"start": v(-16.34, -5.15) * mm, "end": v(-15.75, -5.54) * mm});
            skLineSegment(sketch, "E215", {"start": v(-15.75, -5.54) * mm, "end": v(-14.63, -5.81) * mm});
            skLineSegment(sketch, "E216", {"start": v(-14.63, -5.81) * mm, "end": v(-13.95, -5.84) * mm});
            skLineSegment(sketch, "E217", {"start": v(-13.95, -5.84) * mm, "end": v(-13.7, -5.63) * mm});
            skLineSegment(sketch, "E218", {"start": v(-13.7, -5.63) * mm, "end": v(-13.38, -4.66) * mm});
            skLineSegment(sketch, "E219", {"start": v(-13.38, -4.66) * mm, "end": v(-13.86, -2.83) * mm});
            skLineSegment(sketch, "E220", {"start": v(-13.86, -2.83) * mm, "end": v(-14.75, -0.68) * mm});
            skLineSegment(sketch, "E221", {"start": v(-14.75, -0.68) * mm, "end": v(-15.26, 0) * mm});
            skLineSegment(sketch, "E222", {"start": v(-15.26, 0) * mm, "end": v(-15.82, 0.42) * mm});
            skLineSegment(sketch, "E223", {"start": v(-15.82, 0.42) * mm, "end": v(-16.3, 0.51) * mm});
            skLineSegment(sketch, "E224", {"start": v(-16.3, 0.51) * mm, "end": v(-16.76, 0.35) * mm});
            skLineSegment(sketch, "E225", {"start": v(-16.76, 0.35) * mm, "end": v(-17.15, 0) * mm});
            skLineSegment(sketch, "E226", {"start": v(-17.15, 0) * mm, "end": v(-18, -0.95) * mm});
            skLineSegment(sketch, "E227", {"start": v(-18, -0.95) * mm, "end": v(-18.6, -0.42) * mm});
            skLineSegment(sketch, "E228", {"start": v(-18.6, -0.42) * mm, "end": v(-19.23, 0.16) * mm});
            skLineSegment(sketch, "E229", {"start": v(-19.23, 0.16) * mm, "end": v(-19.87, 1.03) * mm});
            skLineSegment(sketch, "E230", {"start": v(-19.87, 1.03) * mm, "end": v(-20.4, 1.96) * mm});
            skLineSegment(sketch, "E231", {"start": v(-20.4, 1.96) * mm, "end": v(-20.78, 2.78) * mm});
            skLineSegment(sketch, "E232", {"start": v(-20.78, 2.78) * mm, "end": v(-21.05, 3.55) * mm});
            skLineSegment(sketch, "E233", {"start": v(-21.05, 3.55) * mm, "end": v(-21.27, 4.2) * mm});
            skLineSegment(sketch, "E234", {"start": v(-21.27, 4.2) * mm, "end": v(-21.5, 5.07) * mm});
            skLineSegment(sketch, "E235", {"start": v(-21.5, 5.07) * mm, "end": v(-20.69, 4.57) * mm});
            skLineSegment(sketch, "E236", {"start": v(-20.69, 4.57) * mm, "end": v(-20.05, 4.08) * mm});
            skLineSegment(sketch, "E237", {"start": v(-20.05, 4.08) * mm, "end": v(-19.52, 3.8) * mm});
            skLineSegment(sketch, "E238", {"start": v(-19.52, 3.8) * mm, "end": v(-18.87, 3.43) * mm});
            skLineSegment(sketch, "E239", {"start": v(-18.87, 3.43) * mm, "end": v(-18.16, 3.3) * mm});
            skLineSegment(sketch, "E240", {"start": v(-18.16, 3.3) * mm, "end": v(-17.54, 3.3) * mm});
            skLineSegment(sketch, "E241", {"start": v(-17.54, 3.3) * mm, "end": v(-17.12, 3.3) * mm});
            skLineSegment(sketch, "E242", {"start": v(-17.12, 3.3) * mm, "end": v(-17.33, 4.58) * mm});
            skLineSegment(sketch, "E243", {"start": v(-17.33, 4.58) * mm, "end": v(-17.71, 5.6) * mm});
            skLineSegment(sketch, "E244", {"start": v(-17.71, 5.6) * mm, "end": v(-18.19, 6.24) * mm});
            skLineSegment(sketch, "E245", {"start": v(-18.19, 6.24) * mm, "end": v(-18.75, 6.84) * mm});
            skLineSegment(sketch, "E246", {"start": v(-18.75, 6.84) * mm, "end": v(-19.38, 7.25) * mm});
            skLineSegment(sketch, "E247", {"start": v(-19.38, 7.25) * mm, "end": v(-20.17, 7.64) * mm});
            skLineSegment(sketch, "E248", {"start": v(-20.17, 7.64) * mm, "end": v(-20.84, 7.9) * mm});
            skLineSegment(sketch, "E249", {"start": v(-20.84, 7.9) * mm, "end": v(-21.5, 8.06) * mm});
            skLineSegment(sketch, "E250", {"start": v(-21.5, 8.06) * mm, "end": v(-20.7, 9.18) * mm});
            skLineSegment(sketch, "E251", {"start": v(-20.7, 9.18) * mm, "end": v(-19.82, 10.46) * mm});
            skLineSegment(sketch, "E252", {"start": v(-19.82, 10.46) * mm, "end": v(-18.97, 11.63) * mm});
            skLineSegment(sketch, "E253", {"start": v(-18.97, 11.63) * mm, "end": v(-18.1, 12.84) * mm});
            skLineSegment(sketch, "E254", {"start": v(-18.1, 12.84) * mm, "end": v(-17.79, 13.64) * mm});
            skLineSegment(sketch, "E255", {"start": v(-17.79, 13.64) * mm, "end": v(-17.79, 14.8) * mm});
            skLineSegment(sketch, "E256", {"start": v(-17.79, 14.8) * mm, "end": v(-17.62, 17.09) * mm});
            skLineSegment(sketch, "E257", {"start": v(-17.62, 17.09) * mm, "end": v(-16.5, 16.3) * mm});
            skLineSegment(sketch, "E258", {"start": v(-16.5, 16.3) * mm, "end": v(-15.54, 15.66) * mm});
            skLineSegment(sketch, "E259", {"start": v(-15.54, 15.66) * mm, "end": v(-14.87, 15.66) * mm});
            skLineSegment(sketch, "E260", {"start": v(-14.87, 15.66) * mm, "end": v(-14.36, 15.96) * mm});
            skLineSegment(sketch, "E261", {"start": v(-14.36, 15.96) * mm, "end": v(-10.83, 18.96) * mm});
            skLineSegment(sketch, "E262", {"start": v(-10.83, 18.96) * mm, "end": v(-10.4, 19.23) * mm});
            skLineSegment(sketch, "E263", {"start": v(-10.4, 19.23) * mm, "end": v(-10, 19.27) * mm});
            skLineSegment(sketch, "E264", {"start": v(-10, 19.27) * mm, "end": v(-9.6, 19.1) * mm});
            skLineSegment(sketch, "E265", {"start": v(-9.6, 19.1) * mm, "end": v(-5.53, 15.94) * mm});
            skLineSegment(sketch, "E266", {"start": v(-5.53, 15.94) * mm, "end": v(-5.06, 15.74) * mm});
            skLineSegment(sketch, "E267", {"start": v(-5.06, 15.74) * mm, "end": v(-4.49, 15.83) * mm});
            skLineSegment(sketch, "E268", {"start": v(-4.49, 15.83) * mm, "end": v(-2.54, 16.95) * mm});
            skLineSegment(sketch, "E269", {"start": v(-2.54, 16.95) * mm, "end": v(-2.3, 13.9) * mm});
            skLineSegment(sketch, "E270", {"start": v(-2.3, 13.9) * mm, "end": v(-2.1, 13.05) * mm});
            skLineSegment(sketch, "E271", {"start": v(-2.1, 13.05) * mm, "end": v(-1.64, 12.25) * mm});
            skLineSegment(sketch, "E272", {"start": v(-1.64, 12.25) * mm, "end": v(0.9, 8.98) * mm});
            skLineSegment(sketch, "E273", {"start": v(0.9, 8.98) * mm, "end": v(1.3, 8.33) * mm});
            skLineSegment(sketch, "E274", {"start": v(1.3, 8.33) * mm, "end": v(0.3, 7.74) * mm});
            skLineSegment(sketch, "E275", {"start": v(0.3, 7.74) * mm, "end": v(-0.73, 7.11) * mm});
            skLineSegment(sketch, "E276", {"start": v(-0.73, 7.11) * mm, "end": v(-1.71, 6.2) * mm});
            skLineSegment(sketch, "E277", {"start": v(-1.71, 6.2) * mm, "end": v(-2.29, 5.16) * mm});
            skLineSegment(sketch, "E278", {"start": v(-2.29, 5.16) * mm, "end": v(-2.64, 4) * mm});
            skLineSegment(sketch, "E279", {"start": v(-2.64, 4) * mm, "end": v(-2.7, 3.04) * mm});
            skLineSegment(sketch, "E280", {"start": v(-2.7, 3.04) * mm, "end": v(-1.66, 2.99) * mm});
            skLineSegment(sketch, "E281", {"start": v(-1.66, 2.99) * mm, "end": v(-0.65, 3.4) * mm});
            skLineSegment(sketch, "E282", {"start": v(-0.65, 3.4) * mm, "end": v(0.43, 4.12) * mm});
            skLineSegment(sketch, "E283", {"start": v(0.43, 4.12) * mm, "end": v(1.4, 4.9) * mm});
            skLineSegment(sketch, "E284", {"start": v(1.4, 4.9) * mm, "end": v(2, 5.37) * mm});
            skLineSegment(sketch, "E285", {"start": v(2, 5.37) * mm, "end": v(1.39, 3.1) * mm});
            skLineSegment(sketch, "E286", {"start": v(1.39, 3.1) * mm, "end": v(0.33, 1.03) * mm});
            skLineSegment(sketch, "E287", {"start": v(0.33, 1.03) * mm, "end": v(-0.81, -0.88) * mm});
            skLineSegment(sketch, "E288", {"start": v(-0.81, -0.88) * mm, "end": v(-1.45, -1.9) * mm});
            skLineSegment(sketch, "E289", {"start": v(-1.45, -1.9) * mm, "end": v(-2.23, -0.73) * mm});
            skLineSegment(sketch, "E290", {"start": v(-2.23, -0.73) * mm, "end": v(-2.93, 0.1) * mm});
            skLineSegment(sketch, "E291", {"start": v(-2.93, 0.1) * mm, "end": v(-3.3, 0.37) * mm});
            skLineSegment(sketch, "E292", {"start": v(-3.3, 0.37) * mm, "end": v(-3.64, 0.42) * mm});
            skLineSegment(sketch, "E293", {"start": v(-3.64, 0.42) * mm, "end": v(-4.2, 0.22) * mm});
            skLineSegment(sketch, "E294", {"start": v(-4.2, 0.22) * mm, "end": v(-4.8, -0.46) * mm});
            skLineSegment(sketch, "E295", {"start": v(-4.8, -0.46) * mm, "end": v(-5.72, -1.9) * mm});
            skLineSegment(sketch, "E296", {"start": v(-5.72, -1.9) * mm, "end": v(-6.5, -3.82) * mm});
            skLineSegment(sketch, "E297", {"start": v(-6.5, -3.82) * mm, "end": v(-6.87, -5.12) * mm});
            skLineSegment(sketch, "E298", {"start": v(-6.87, -5.12) * mm, "end": v(-7.07, -6.6) * mm});
            skLineSegment(sketch, "E299", {"start": v(-7.07, -6.6) * mm, "end": v(-7.15, -8.07) * mm});
            skLineSegment(sketch, "E300", {"start": v(-7.15, -8.07) * mm, "end": v(-6.91, -8.94) * mm});
            skLineSegment(sketch, "E301", {"start": v(-6.91, -8.94) * mm, "end": v(-6.23, -9.73) * mm});
            skLineSegment(sketch, "E302", {"start": v(-6.23, -9.73) * mm, "end": v(-5.31, -10.18) * mm});
            skLineSegment(sketch, "E303", {"start": v(-5.31, -10.18) * mm, "end": v(-4.64, -10.39) * mm});
            skLineSegment(sketch, "E304", {"start": v(-4.64, -10.39) * mm, "end": v(-5.36, -11.28) * mm});
            skLineSegment(sketch, "E305", {"start": v(-5.36, -11.28) * mm, "end": v(-6.08, -12.41) * mm});
            skLineSegment(sketch, "E306", {"start": v(-6.08, -12.41) * mm, "end": v(-6.6, -13.56) * mm});
            skLineSegment(sketch, "E307", {"start": v(-6.6, -13.56) * mm, "end": v(-7.22, -15.58) * mm});
            skLineSegment(sketch, "E308", {"start": v(-7.22, -15.58) * mm, "end": v(-7.73, -18.14) * mm});
            skLineSegment(sketch, "E309", {"start": v(-8.46, -19.92) * mm, "end": v(-8.63, -18.49) * mm});
            skLineSegment(sketch, "E310", {"start": v(-8.63, -18.49) * mm, "end": v(-8.54, -14.27) * mm});
            skLineSegment(sketch, "E311", {"start": v(-8.54, -14.27) * mm, "end": v(-8.43, -10.75) * mm});
            skLineSegment(sketch, "E312", {"start": v(-8.43, -10.75) * mm, "end": v(-8.27, -5.73) * mm});
            skLineSegment(sketch, "E313", {"start": v(-8.27, -5.73) * mm, "end": v(-8.08, -2.45) * mm});
            skLineSegment(sketch, "E314", {"start": v(-8.08, -2.45) * mm, "end": v(-7.82, -1.26) * mm});
            skLineSegment(sketch, "E315", {"start": v(-7.82, -1.26) * mm, "end": v(-7.29, 0) * mm});
            skLineSegment(sketch, "E316", {"start": v(-7.29, 0) * mm, "end": v(-6.39, 1.39) * mm});
            skLineSegment(sketch, "E317", {"start": v(-6.39, 1.39) * mm, "end": v(-5.66, 2.54) * mm});
            skLineSegment(sketch, "E318", {"start": v(-5.66, 2.54) * mm, "end": v(-5.16, 3.77) * mm});
            skLineSegment(sketch, "E319", {"start": v(-5.16, 3.77) * mm, "end": v(-4.77, 5.2) * mm});
            skLineSegment(sketch, "E320", {"start": v(-4.77, 5.2) * mm, "end": v(-4.65, 6.06) * mm});
            skLineSegment(sketch, "E321", {"start": v(-4.65, 6.06) * mm, "end": v(-4.63, 7.09) * mm});
            skLineSegment(sketch, "E322", {"start": v(-4.63, 7.09) * mm, "end": v(-4.84, 8.27) * mm});
            skLineSegment(sketch, "E323", {"start": v(-4.84, 8.27) * mm, "end": v(-5.23, 9.48) * mm});
            skLineSegment(sketch, "E324", {"start": v(-5.23, 9.48) * mm, "end": v(-5.91, 10.64) * mm});
            skLineSegment(sketch, "E325", {"start": v(-5.91, 10.64) * mm, "end": v(-7.12, 11.76) * mm});
            skLineSegment(sketch, "E326", {"start": v(-7.12, 11.76) * mm, "end": v(-7.93, 12.36) * mm});
            skLineSegment(sketch, "E327", {"start": v(-7.93, 12.36) * mm, "end": v(-8.91, 12.85) * mm});
            skLineSegment(sketch, "E328", {"start": v(-8.91, 12.85) * mm, "end": v(-9.88, 13.32) * mm});
            skLineSegment(sketch, "E329", {"start": v(-9.88, 13.32) * mm, "end": v(-10.42, 13.36) * mm});
            skLineSegment(sketch, "E330", {"start": v(-10.42, 13.36) * mm, "end": v(-11.47, 12.97) * mm});
            skLineSegment(sketch, "E331", {"start": v(-11.47, 12.97) * mm, "end": v(-12.7, 12.24) * mm});
            skLineSegment(sketch, "E332", {"start": v(-12.7, 12.24) * mm, "end": v(-13.55, 11.57) * mm});
            skLineSegment(sketch, "E333", {"start": v(-13.55, 11.57) * mm, "end": v(-14.53, 10.54) * mm});
            skLineSegment(sketch, "E334", {"start": v(-14.53, 10.54) * mm, "end": v(-15.22, 9.19) * mm});
            skLineSegment(sketch, "E335", {"start": v(-15.22, 9.19) * mm, "end": v(-15.46, 8.3) * mm});
            skLineSegment(sketch, "E336", {"start": v(-15.46, 8.3) * mm, "end": v(-15.68, 7.4) * mm});
            skLineSegment(sketch, "E337", {"start": v(-15.68, 7.4) * mm, "end": v(-15.66, 6.12) * mm});
            skLineSegment(sketch, "E338", {"start": v(-15.66, 6.12) * mm, "end": v(-15.3, 4.53) * mm});
            skLineSegment(sketch, "E339", {"start": v(-15.3, 4.53) * mm, "end": v(-14.72, 3.21) * mm});
            skLineSegment(sketch, "E340", {"start": v(-14.72, 3.21) * mm, "end": v(-13.92, 1.94) * mm});
            skLineSegment(sketch, "E341", {"start": v(-13.92, 1.94) * mm, "end": v(-13.07, 0.6) * mm});
            skLineSegment(sketch, "E342", {"start": v(-13.07, 0.6) * mm, "end": v(-12.34, -1.1) * mm});
            skLineSegment(sketch, "E343", {"start": v(-12.34, -1.1) * mm, "end": v(-11.7, -3.06) * mm});
            skLineSegment(sketch, "E344", {"start": v(-11.7, -3.06) * mm, "end": v(-11.33, -5.07) * mm});
            skLineSegment(sketch, "E345", {"start": v(-11.33, -5.07) * mm, "end": v(-11.02, -7.2) * mm});
            skLineSegment(sketch, "E346", {"start": v(-11.02, -7.2) * mm, "end": v(-10.9, -7.97) * mm});
            skLineSegment(sketch, "E347", {"start": v(-10.9, -7.97) * mm, "end": v(-10.9, -8.7) * mm});
            skLineSegment(sketch, "E348", {"start": v(-10.9, -8.7) * mm, "end": v(-11.25, -10.41) * mm});
            skLineSegment(sketch, "E349", {"start": v(-11.25, -10.41) * mm, "end": v(-12.16, -12.96) * mm});
            skLineSegment(sketch, "E350", {"start": v(-12.16, -12.96) * mm, "end": v(-13.61, -11.2) * mm});
            skLineSegment(sketch, "E351", {"start": v(-13.61, -11.2) * mm, "end": v(-14.43, -9.89) * mm});
            skLineSegment(sketch, "E352", {"start": v(-14.43, -9.89) * mm, "end": v(-14.95, -8.95) * mm});
            skLineSegment(sketch, "E353", {"start": v(-14.95, -8.95) * mm, "end": v(-15.51, -7.6) * mm});
            skLineSegment(sketch, "E354", {"start": v(-15.51, -7.6) * mm, "end": v(-16, -6.25) * mm});
            skLineSegment(sketch, "E355", {"start": v(-16, -6.25) * mm, "end": v(-16.34, -5.15) * mm});
            skLineSegment(sketch, "E356", {"start": v(-8.46, -19.92) * mm, "end": v(-7.73, -18.14) * mm});
            skSolve(sketch);
        }
        {
            var Q0;
            Q0 = qSketchRegion(id + "F6", true);
            extrude(context, id + "F8", {"entities" : qUnion([Q0]), "operationType" : NewBodyOperationType.ADD, "depth" : 5 * mm});
        }
        {
            var Q0;
            Q0 = qSketchRegion(id + "F7", true);
            extrude(context, id + "F9", {"entities" : qUnion([Q0]), "operationType" : NewBodyOperationType.ADD, "depth" : 5 * mm});
        }
        {
            var Q0;
            Q0 = qSketchRegion(id + "F5", true);
            var Q1;
            Q1=makeQuery(id+"F5.imprint","IMPRINT",FACE,{"disambiguationData":[TD([[makeQuery(id+"F5.imprint","IMPRINT",EDGE,{"derivedFrom":sQuery(id+"F5.wireOp",EDGE,"E4")}),1.0]])]});
            extrude(context, id + "F10", {"entities" : qUnion([Q0, Q1]), "operationType" : NewBodyOperationType.ADD, "depth" : 5 * mm});
        }
    });
